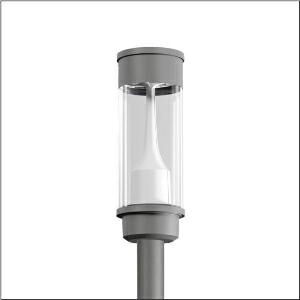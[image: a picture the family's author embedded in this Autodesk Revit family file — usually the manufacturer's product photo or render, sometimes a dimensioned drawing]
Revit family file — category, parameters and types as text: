
# Revit family: litepole_iq___st1_2a_5xa5415ef14h_6754
name_source: partatom
category: Lighting Fixtures
units: mm (PartAtom-declared; Revit-internal decimal feet)

## family parameters
Cut with Voids When Loaded = No
Host = Face
Light Source = No
Part Type = Normal
Room Calculation Point = No
Round Connector Dimension = Use Diameter
Shared = No

## types (1)
- --- (1 x LED, 1540 lm, 10.5 W, 3000K)
    Apparent Load = 11 VA
    CIE Flux Codes = 22 61 93 96 100
    Color Rendering = 70
    Color Temperature = 3000K
    Default Elevation = 1800 mm
    Description = Litepole iQ, mast luminaire, Module 540 iQ-SR, primary light control with 3 zone facetted reflector, of plastic, silver coated, highly specular, structured, primary optical cover: cover, of PMMA, transparent, light distribution: ST1.2a, light emission: direct distribution, primary light characteristic: asymmetric, installation type: post-top, LED, High Power LED, rated luminous flux: 1.540lm, luminous efficacy: 147lm/W, light colour: 730, colour temperature: 3000K, control gear: ECG iQ, control: Auto-Match, Temp-Guard, Lumen-Switch, Night-Set, Smart-Wire, Light-Fading, Desk-Remote (wireless, voltage-free reading and setting of iQ features in the workshop via application-optimized NFC function/RFID function), optimised constant luminous flux control (CLO 2.0), Street-Remote, presetting dimming logarithmic, with terminal, 6-pole, max. 2.5mm², mains connection: 230..240V, AC, 50/60Hz, start of lifetime: 11W, end of service life: 11W, reduction: 5W, luminaire housing, upper part, of glass-fibre reinforced polyester, coated, Siteco® metallic grey (DB 702S), diameter: 210mm, height: 590mm, spigot size: d x l = 76 x 70mm (post-top) | with reducer (optional accessory) 60 x 70mm, post-top mast mounting element, of diecast aluminium, coated, Siteco® metallic grey (DB 702S), Module 540 iQ-SR, traffic white (RAL 9016), equipment: standard, protection rating (complete): IP65, insulation class (complete): insulation class II (safety insulation), certification: CE, ENEC, VDE, packaging unit: 1 piece

Light Distribution: ST1.2a
    Height = 590 mm
    Lamp = 1 x LED
    Lamp Light Flux = 1540 lm
    Lamp Power = 10.5 W
    Lamp count = 1
    Length = 220 mm
    Luminous efficacy = 147 lm/W
    Manufacturer = Siteco
    ModVariant = No
    Model = 5XA5415EF14H
    Number of Poles = 1
    OnlyDefault = Yes
    Power Factor = 1
    Product Name = Litepole iQ | ST1.2a
    Product group = mast luminaire | pylon top
    ProductGroupID = 6100
    Protection Class = Protection class II
    Protection Degree = IP 65
    RLX_Detail_Level = 1
    RLX_Emergency_Light_Flux = 0 lm
    RLX_Emergency_Type = 0
    RLX_Emergency_Type_DB = No
    RlxData = <blob elided: 71813 chars, md5=a72282bc>
    Socket = socket
    Standby Power = 0 W
    System Light Flux = 1540 lm
    System Power = 11 W
    Type Comments = factory setting: luminous flux: 100 % | dim-lin: 254 | 419 mA
    Type Image = l_1006025.jpg
    URL = http://relux.com
    VarID = @adj_109035
    Voltage = 0 V
    Weight = 0.00 kg
    Width = 0 mm  [stored 0 ft]

note: [stored X ft] marks values corroborated as IEEE doubles in the binary element streams (Revit-internal decimal feet)

## geometry (parser evidence)
native form markers: Blend x4, Sweep x11
no freeform markers — native parametric forms only
